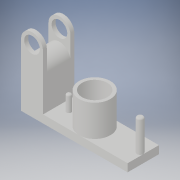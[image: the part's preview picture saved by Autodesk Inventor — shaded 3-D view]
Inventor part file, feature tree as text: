
AUTODESK INVENTOR PART (.ipt)
format: ipt  version: 2019 (Build 230136000, 136)  size: 184,832 bytes
history: native  units: in
note: dims shown in document units (in); Inventor stores cm internally (conversion verified against a paired STEP export)
features: sketch x6, extrude x5, fillet x3
ambient origin geometry x8: Origin, YZ Plane, XZ Plane, XY Plane, X Axis, Y Axis, Z Axis, Center Point
bodies: Solid1 (feature_tree)
feature tree (14):
  extrude  "Extrusion1"  Depth=0.1969in
  extrude  "Extrusion2"  Depth=0.3937in
  extrude  "Extrusion3"  Depth=2.126in
  fillet  "Fillet1"  Radius=0.7874in
  fillet  "Fillet2"  Radius=0.1181in
  extrude  "Extrusion4"  Depth=0.7874in
  sketch  "Sketch6"  dims[d13=0.2559in d14=0.7874in]
  extrude  "Extrusion5"  Depth=0.3937in
  fillet  "Fillet3"  Radius=0.1575in
  sketch  "Sketch8"  dims[d21=0.3937in d22=0.6693in d23=0.7874in d24=0.0in d25=0.3937in d26=0.7874in d27=0.0in d28=0.0394in d29=0.0394in d30=0.6299in d31=1.1811in d32=0.0in d40=0.5512in d41=0.5512in d42=0.5906in d43=0.5512in d44=0.0in d45=0.2756in d46=2.6772in d47=1.2205in d48=2.3228in d49=1.1811in]
  sketch  "Sketch1"  dims[d0=1.5748in d2=0.1969in]
  sketch  "Sketch4"  dims[d6=0.2756in d7=0.3937in]
  sketch  "Sketch5"  dims[d8=0.5512in d9=2.126in d10=0.7874in d11=0.0in d12=0.1181in]
  sketch  "Sketch7"  dims[d16=0.9055in d19=0.3937in d20=0.1575in]
